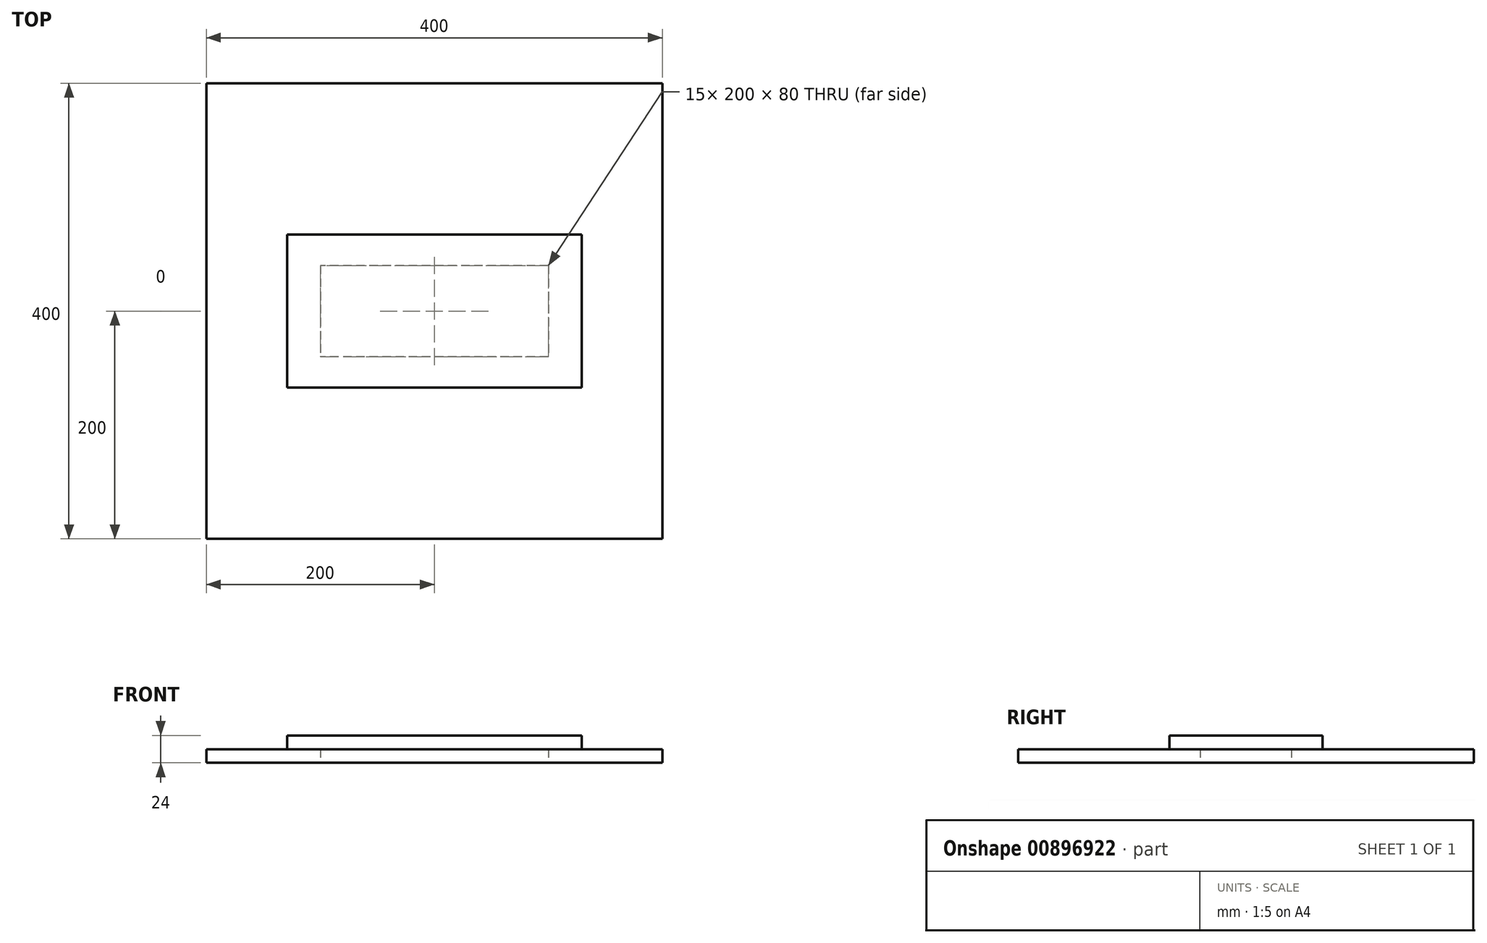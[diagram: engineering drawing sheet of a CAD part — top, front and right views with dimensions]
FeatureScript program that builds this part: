
annotation { "Feature Type Name" : "Feature", "Feature Type Description" : "" }
export const myFeature = defineFeature(function(context is Context, id is Id, definition is map)
    precondition{}
    {
        {
            var Q0;
            Q0=qCreatedBy(makeId("Top.planeOp"),FACE);
            var sketch = newSketch(context, id + "F0", { "sketchPlane" : qUnion([Q0])});
            skLineSegment(sketch, "E0.bottom", {"start": v(200, 200) * mm, "end": v(-200, 200) * mm});
            skLineSegment(sketch, "E0.top", {"start": v(200, -200) * mm, "end": v(-200, -200) * mm});
            skLineSegment(sketch, "E0.left", {"start": v(200, 200) * mm, "end": v(200, -200) * mm});
            skLineSegment(sketch, "E0.right", {"start": v(-200, 200) * mm, "end": v(-200, -200) * mm});
            skPoint(sketch, "E0.middle", {"position": v(0, 0) * mm});
            skLineSegment(sketch, "E1.bottom", {"start": v(100, 40) * mm, "end": v(-100, 40) * mm});
            skLineSegment(sketch, "E1.top", {"start": v(100, -40) * mm, "end": v(-100, -40) * mm});
            skLineSegment(sketch, "E1.left", {"start": v(100, 40) * mm, "end": v(100, -40) * mm});
            skLineSegment(sketch, "E1.right", {"start": v(-100, 40) * mm, "end": v(-100, -40) * mm});
            skSolve(sketch);
        }
        {
            var Q0;
            Q0 = qSketchRegion(id + "F0", true);
            extrude(context, id + "F1", {"entities" : qUnion([Q0]), "depth" : 12 * mm, "offsetDistance" : 25 * mm});
        }
        {
            var Q0;
            Q0=makeQuery(id+"F1.opExtrude","CAP_FACE",FACE,{"disambiguationData":[OSD([sQuery(id+"F0.wireOp",EDGE,"E0.bottom"),sQuery(id+"F0.wireOp",EDGE,"E0.top"),sQuery(id+"F0.wireOp",EDGE,"E0.left"),sQuery(id+"F0.wireOp",EDGE,"E0.right"),sQuery(id+"F0.wireOp",EDGE,"E1.bottom"),sQuery(id+"F0.wireOp",EDGE,"E1.top"),sQuery(id+"F0.wireOp",EDGE,"E1.left"),sQuery(id+"F0.wireOp",EDGE,"E1.right")])],"isStart":false});
            var sketch = newSketch(context, id + "F2", { "sketchPlane" : qUnion([Q0])});
            skLineSegment(sketch, "E2.bottom", {"start": v(129.23, 67.23) * mm, "end": v(-129.23, 67.23) * mm});
            skLineSegment(sketch, "E2.top", {"start": v(129.23, -67.23) * mm, "end": v(-129.23, -67.23) * mm});
            skLineSegment(sketch, "E2.left", {"start": v(129.23, 67.23) * mm, "end": v(129.23, -67.23) * mm});
            skLineSegment(sketch, "E2.right", {"start": v(-129.23, 67.23) * mm, "end": v(-129.23, -67.23) * mm});
            skPoint(sketch, "E2.middle", {"position": v(0, 0) * mm});
            skSolve(sketch);
        }
        {
            var Q0;
            Q0=makeQuery(id+"F2.imprint","IMPRINT",FACE,{"disambiguationData":[TD([[makeQuery(id+"F2.imprint","IMPRINT",EDGE,{"derivedFrom":sQuery(id+"F2.wireOp",EDGE,"E2.bottom")}),1.0]])]});
            var Q1;
            Q1=makeQuery(id+"F2.imprint","IMPRINT",FACE,{"disambiguationData":[TD([[makeQuery(id+"F2.imprint","IMPRINT",EDGE,{"derivedFrom":makeQuery(id+"F1.opExtrude","CAP_EDGE",EDGE,{"disambiguationData":[OSD([sQuery(id+"F0.wireOp",EDGE,"E1.bottom")])],"isStart":false})}),1.0]])]});
            extrude(context, id + "F3", {"entities" : qUnion([Q0, Q1]), "depth" : 12 * mm, "offsetDistance" : 25 * mm});
        }
    });
